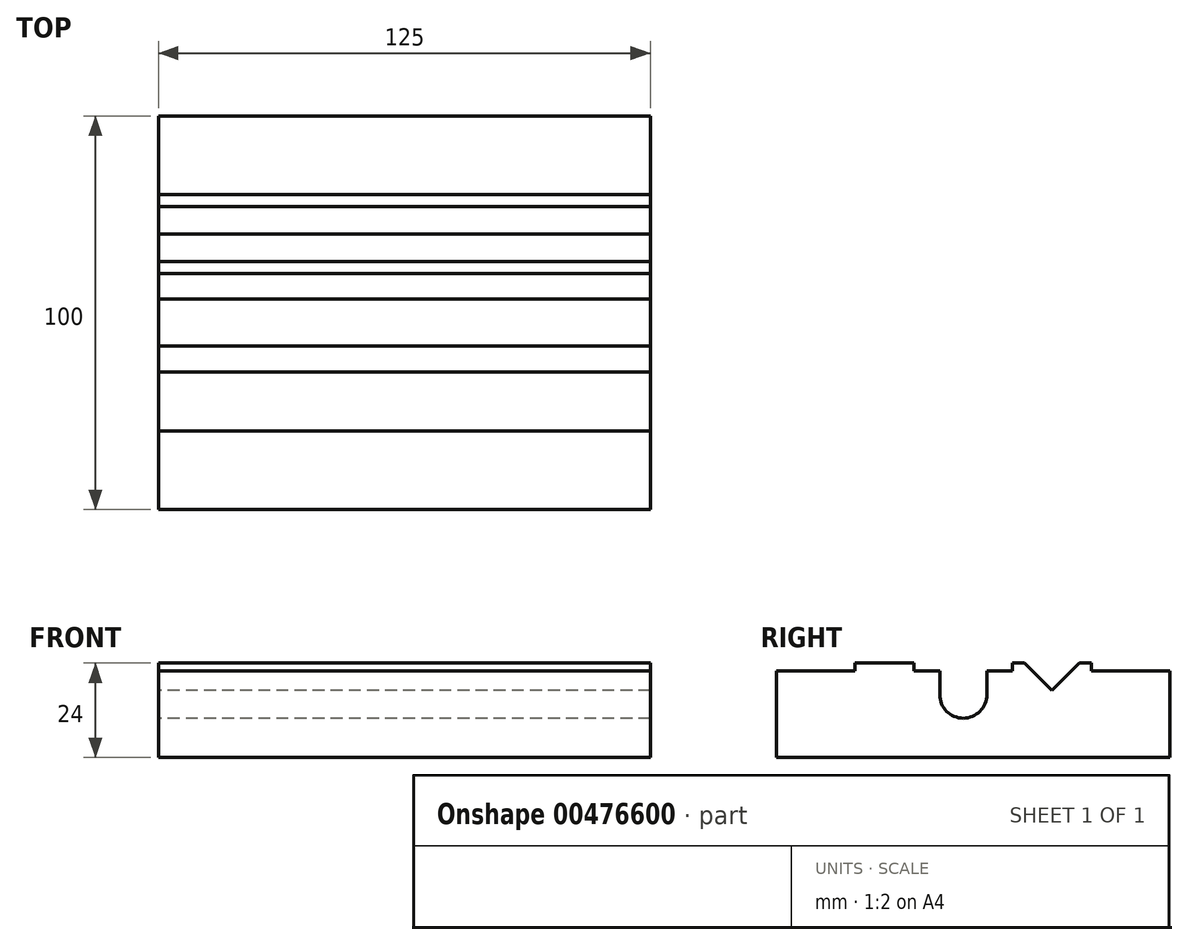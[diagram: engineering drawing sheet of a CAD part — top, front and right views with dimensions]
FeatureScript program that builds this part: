
annotation { "Feature Type Name" : "Feature", "Feature Type Description" : "" }
export const myFeature = defineFeature(function(context is Context, id is Id, definition is map)
    precondition{}
    {
        {
            var Q0;
            Q0=qCreatedBy(makeId("Right.planeOp"),FACE);
            var sketch = newSketch(context, id + "F0", { "sketchPlane" : qUnion([Q0])});
            skLineSegment(sketch, "E0.bottom", {"start": v(50, 11) * mm, "end": v(30, 11) * mm});
            skLineSegment(sketch, "E0.top", {"start": v(50, -11) * mm, "end": v(-50, -11) * mm});
            skLineSegment(sketch, "E0.left", {"start": v(50, 11) * mm, "end": v(50, -11) * mm});
            skLineSegment(sketch, "E0.right", {"start": v(-50, 11) * mm, "end": v(-50, -11) * mm});
            skPoint(sketch, "E0.middle", {"position": v(0, 0) * mm});
            skLineSegment(sketch, "E1", {"start": v(-30, 11) * mm, "end": v(-30, 13) * mm});
            skLineSegment(sketch, "E2", {"start": v(-30, 13) * mm, "end": v(-15, 13) * mm});
            skLineSegment(sketch, "E3", {"start": v(-15, 13) * mm, "end": v(-15, 11) * mm});
            skLineSegment(sketch, "E4", {"start": v(30, 11) * mm, "end": v(30, 13) * mm});
            skLineSegment(sketch, "E5", {"start": v(30, 13) * mm, "end": v(27, 13) * mm});
            skLineSegment(sketch, "E6", {"start": v(27, 13) * mm, "end": v(20, 6) * mm});
            skLineSegment(sketch, "E7", {"start": v(20, 6) * mm, "end": v(13, 13) * mm});
            skLineSegment(sketch, "E8", {"start": v(13, 13) * mm, "end": v(10, 13) * mm});
            skLineSegment(sketch, "E9", {"start": v(10, 13) * mm, "end": v(10, 11) * mm});
            skLineSegment(sketch, "E10.trimOffspring", {"start": v(-30, 11) * mm, "end": v(-50, 11) * mm});
            skLineSegment(sketch, "E11.trimOffspring", {"start": v(10, 11) * mm, "end": v(3.5, 11) * mm});
            skLineSegment(sketch, "E12", {"start": v(20, 6) * mm, "end": v(20, 44.08) * mm, "construction": true});
            skLineSegment(sketch, "E13", {"start": v(-22.5, 42.6) * mm, "end": v(-22.5, -53.03) * mm, "construction": true});
            skArc(sketch, "E14", {"start": v(-8.5, 5) * mm, "mid": v(-2.5, -1) * mm, "end": v(3.5, 5) * mm});
            skLineSegment(sketch, "E15", {"start": v(-8.5, 5) * mm, "end": v(-8.5, 11) * mm});
            skLineSegment(sketch, "E16", {"start": v(3.5, 5) * mm, "end": v(3.5, 11) * mm});
            skLineSegment(sketch, "E17.trimOffspring", {"start": v(-8.5, 11) * mm, "end": v(-15, 11) * mm});
            skSolve(sketch);
        }
        {
            var Q0;
            Q0=makeQuery(id+"F0.imprint","IMPRINT",FACE,{"disambiguationData":[TD([[makeQuery(id+"F0.imprint","IMPRINT",EDGE,{"derivedFrom":sQuery(id+"F0.wireOp",EDGE,"E0.bottom")}),1.0]])]});
            extrude(context, id + "F1", {"entities" : qUnion([Q0]), "depth" : 125 * mm});
        }
    });
